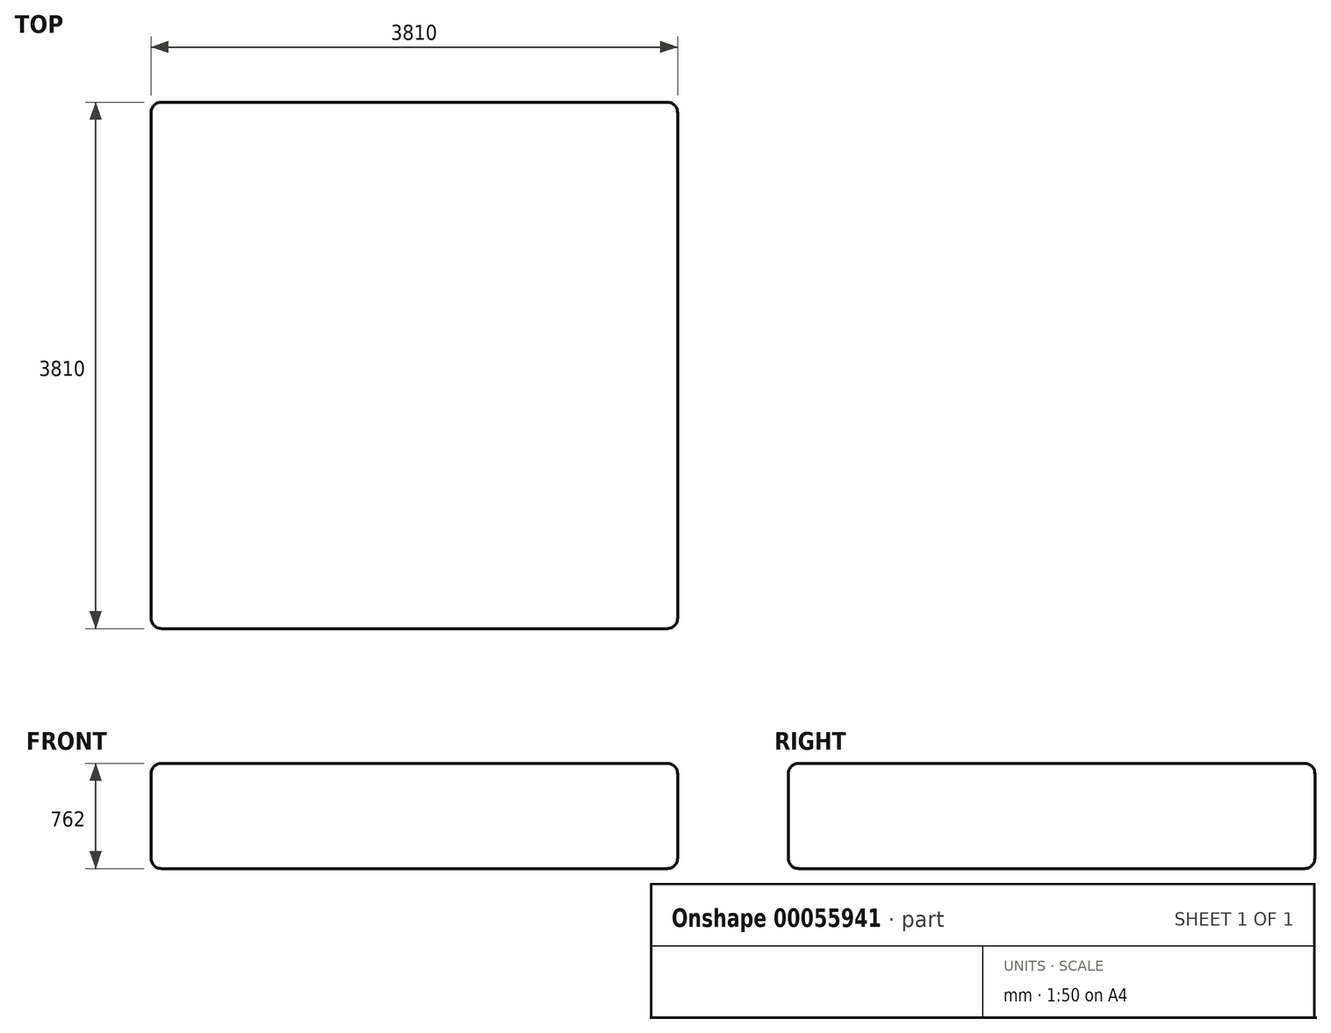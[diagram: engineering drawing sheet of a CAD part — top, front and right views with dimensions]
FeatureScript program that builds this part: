
annotation { "Feature Type Name" : "Feature", "Feature Type Description" : "" }
export const myFeature = defineFeature(function(context is Context, id is Id, definition is map)
    precondition{}
    {
        {
            var Q0;
            Q0=qCreatedBy(makeId("Front.planeOp"),FACE);
            var sketch = newSketch(context, id + "F0", { "sketchPlane" : qUnion([Q0])});
            skLineSegment(sketch, "E0", {"start": v(-1228.85, 421.65) * mm, "end": v(2581.15, 421.65) * mm});
            skLineSegment(sketch, "E1", {"start": v(2581.15, 421.65) * mm, "end": v(2581.15, -340.35) * mm});
            skLineSegment(sketch, "E2", {"start": v(2581.15, -340.35) * mm, "end": v(-1228.85, -340.35) * mm});
            skLineSegment(sketch, "E3", {"start": v(-1228.85, -340.35) * mm, "end": v(-1228.85, 421.65) * mm});
            skSolve(sketch);
        }
        {
            var Q0;
            Q0 = qSketchRegion(id + "F0", true);
            var Q1;
            Q1=makeQuery(id+"F0.imprint","IMPRINT",FACE,{"disambiguationData":[TD([[makeQuery(id+"F0.imprint","IMPRINT",EDGE,{"derivedFrom":sQuery(id+"F0.wireOp",EDGE,"E0")}),-1.0]])]});
            extrude(context, id + "F1", {"entities" : qUnion([Q0, Q1]), "depth" : 3810 * mm});
        }
        {
            var Q0;
            Q0=makeQuery(id+"F1.opExtrude","CAP_EDGE",EDGE,{"disambiguationData":[OSD([sQuery(id+"F0.wireOp",EDGE,"E2")])],"isStart":false});
            var Q1;
            Q1=makeQuery(id+"F1.opExtrude","SWEPT_EDGE",EDGE,{"disambiguationData":[OSD([sQuery(id+"F0.wireOp",EDGE,"E2"),sQuery(id+"F0.wireOp",EDGE,"E3")])]});
            var Q2;
            Q2=makeQuery(id+"F1.opExtrude","CAP_EDGE",EDGE,{"disambiguationData":[OSD([sQuery(id+"F0.wireOp",EDGE,"E2")])],"isStart":true});
            var Q3;
            Q3=makeQuery(id+"F1.opExtrude","SWEPT_EDGE",EDGE,{"disambiguationData":[OSD([sQuery(id+"F0.wireOp",EDGE,"E1"),sQuery(id+"F0.wireOp",EDGE,"E2")])]});
            var Q4;
            Q4=makeQuery(id+"F1.opExtrude","CAP_EDGE",EDGE,{"disambiguationData":[OSD([sQuery(id+"F0.wireOp",EDGE,"E3")])],"isStart":true});
            var Q5;
            Q5=makeQuery(id+"F1.opExtrude","CAP_EDGE",EDGE,{"disambiguationData":[OSD([sQuery(id+"F0.wireOp",EDGE,"E3")])],"isStart":false});
            var Q6;
            Q6=makeQuery(id+"F1.opExtrude","CAP_EDGE",EDGE,{"disambiguationData":[OSD([sQuery(id+"F0.wireOp",EDGE,"E1")])],"isStart":true});
            var Q7;
            Q7=makeQuery(id+"F1.opExtrude","CAP_EDGE",EDGE,{"disambiguationData":[OSD([sQuery(id+"F0.wireOp",EDGE,"E1")])],"isStart":false});
            var Q8;
            Q8=makeQuery(id+"F1.opExtrude","CAP_EDGE",EDGE,{"disambiguationData":[OSD([sQuery(id+"F0.wireOp",EDGE,"E0")])],"isStart":false});
            var Q9;
            Q9=makeQuery(id+"F1.opExtrude","SWEPT_EDGE",EDGE,{"disambiguationData":[OSD([sQuery(id+"F0.wireOp",EDGE,"E0"),sQuery(id+"F0.wireOp",EDGE,"E3")])]});
            var Q10;
            Q10=makeQuery(id+"F1.opExtrude","CAP_EDGE",EDGE,{"disambiguationData":[OSD([sQuery(id+"F0.wireOp",EDGE,"E0")])],"isStart":true});
            var Q11;
            Q11=makeQuery(id+"F1.opExtrude","SWEPT_EDGE",EDGE,{"disambiguationData":[OSD([sQuery(id+"F0.wireOp",EDGE,"E0"),sQuery(id+"F0.wireOp",EDGE,"E1")])]});
            fillet(context, id + "F2", {"entities" : qUnion([Q0, Q1, Q2, Q3, Q4, Q5, Q6, Q7, Q8, Q9, Q10, Q11]), "radius" : 76.2 * mm, "tangentPropagation" : true, "allowEdgeOverflow" : false});
        }
    });
